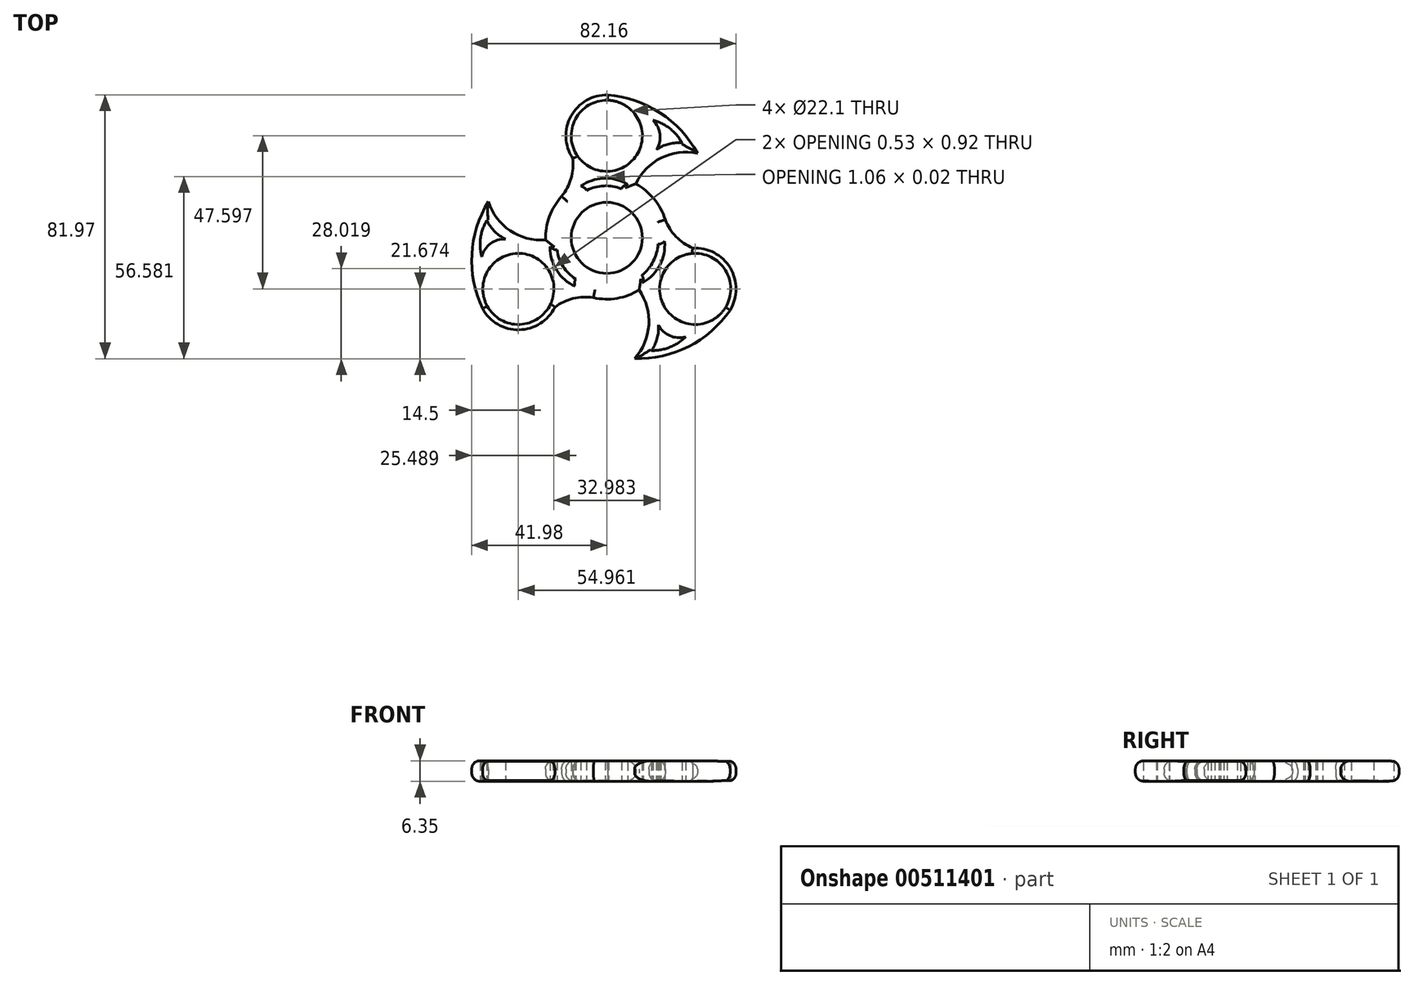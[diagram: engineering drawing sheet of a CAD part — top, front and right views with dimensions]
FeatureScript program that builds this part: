
annotation { "Feature Type Name" : "Feature", "Feature Type Description" : "" }
export const myFeature = defineFeature(function(context is Context, id is Id, definition is map)
    precondition{}
    {
        {
            var Q0;
            Q0=qCreatedBy(makeId("Top.planeOp"),FACE);
            var sketch = newSketch(context, id + "F0", { "sketchPlane" : qUnion([Q0])});
            skCircle(sketch, "E0", {"center": v(0, 0) * mm, "radius": 11.05 * mm});
            skCircle(sketch, "E1", {"center": v(0, 0) * mm, "radius": 44.45 * mm});
            skCircle(sketch, "E2", {"center": v(0, 31.73) * mm, "radius": 11.05 * mm});
            skArc(sketch, "E3", {"start": v(2.6, 44.16) * mm, "mid": v(-10.5, 38.87) * mm, "end": v(-10.6, 24.73) * mm});
            skCircle(sketch, "E4.1.0", {"center": v(-27.48, -15.87) * mm, "radius": 11.05 * mm});
            skArc(sketch, "E4.1.1", {"start": v(-39.55, -19.82) * mm, "mid": v(-28.41, -28.53) * mm, "end": v(-16.12, -21.54) * mm});
            skCircle(sketch, "E4.2.0", {"center": v(27.48, -15.87) * mm, "radius": 11.05 * mm});
            skArc(sketch, "E4.2.1", {"start": v(16.76, -9.06) * mm, "mid": v(16.48, -9.52) * mm, "end": v(16.23, -9.98) * mm});
            skArc(sketch, "E5", {"start": v(28.18, 26.24) * mm, "mid": v(16.42, 38.95) * mm, "end": v(0, 44.45) * mm});
            skArc(sketch, "E6", {"start": v(28.18, 26.24) * mm, "mid": v(16.94, 24.86) * mm, "end": v(9, 16.8) * mm});
            skArc(sketch, "E7.0", {"start": v(-14.02, 12.9) * mm, "mid": v(-17.86, 6.64) * mm, "end": v(-19.04, -0.61) * mm});
            skArc(sketch, "E8", {"start": v(-4.16, -18.6) * mm, "mid": v(-10.44, -18.85) * mm, "end": v(-16.12, -21.54) * mm});
            skArc(sketch, "E9.1.0", {"start": v(-36.82, 11.28) * mm, "mid": v(-41.94, -5.26) * mm, "end": v(-38.5, -22.22) * mm});
            skArc(sketch, "E9.1.1", {"start": v(-36.82, 11.28) * mm, "mid": v(-30, 2.24) * mm, "end": v(-19.04, -0.61) * mm});
            skArc(sketch, "E9.1.2", {"start": v(18.18, 5.7) * mm, "mid": v(21.54, 0.38) * mm, "end": v(26.72, -3.19) * mm});
            skArc(sketch, "E9.2.0", {"start": v(8.64, -37.52) * mm, "mid": v(25.52, -33.7) * mm, "end": v(38.5, -22.23) * mm});
            skArc(sketch, "E9.2.1", {"start": v(8.64, -37.52) * mm, "mid": v(13.06, -27.1) * mm, "end": v(10.05, -16.18) * mm});
            skArc(sketch, "E9.2.2", {"start": v(-14.02, 12.9) * mm, "mid": v(-11.1, 18.47) * mm, "end": v(-10.6, 24.73) * mm});
            skArc(sketch, "E10.trimOffspring", {"start": v(0.53, 19.04) * mm, "mid": v(0, 19.05) * mm, "end": v(-0.53, 19.04) * mm});
            skArc(sketch, "E11.trimOffspring", {"start": v(18.18, 5.7) * mm, "mid": v(14.68, 12.15) * mm, "end": v(9, 16.8) * mm});
            skArc(sketch, "E12.trimOffspring", {"start": v(16.23, -9.98) * mm, "mid": v(16.5, -9.53) * mm, "end": v(16.76, -9.06) * mm});
            skArc(sketch, "E13.trimOffspring", {"start": v(-4.16, -18.6) * mm, "mid": v(3.18, -18.78) * mm, "end": v(10.05, -16.18) * mm});
            skArc(sketch, "E14.trimOffspring", {"start": v(-16.76, -9.06) * mm, "mid": v(-16.5, -9.52) * mm, "end": v(-16.23, -9.98) * mm});
            skArc(sketch, "E15", {"start": v(6.5, 16.58) * mm, "mid": v(-0.86, 18.52) * mm, "end": v(-8.07, 16.08) * mm});
            skArc(sketch, "E16", {"start": v(-6.27, 14.78) * mm, "mid": v(-7.03, 15.62) * mm, "end": v(-8.07, 16.08) * mm});
            skArc(sketch, "E17", {"start": v(4.58, 15.27) * mm, "mid": v(-0.9, 16.16) * mm, "end": v(-6.27, 14.78) * mm});
            skArc(sketch, "E18", {"start": v(6.5, 16.58) * mm, "mid": v(5.35, 16.2) * mm, "end": v(4.58, 15.27) * mm});
            skArc(sketch, "E19.1.0", {"start": v(-17.6, -2.66) * mm, "mid": v(-15.6, -10) * mm, "end": v(-9.9, -15.03) * mm});
            skArc(sketch, "E19.1.1", {"start": v(-17.6, -2.66) * mm, "mid": v(-16.7, -3.46) * mm, "end": v(-15.51, -3.67) * mm});
            skArc(sketch, "E19.1.2", {"start": v(-15.51, -3.67) * mm, "mid": v(-13.55, -8.86) * mm, "end": v(-9.66, -12.82) * mm});
            skArc(sketch, "E19.1.3", {"start": v(-9.66, -12.82) * mm, "mid": v(-10.01, -13.9) * mm, "end": v(-9.9, -15.03) * mm});
            skArc(sketch, "E19.2.0", {"start": v(11.1, -13.92) * mm, "mid": v(16.47, -8.51) * mm, "end": v(17.96, -1.05) * mm});
            skArc(sketch, "E19.2.1", {"start": v(11.1, -13.92) * mm, "mid": v(11.35, -12.73) * mm, "end": v(10.94, -11.6) * mm});
            skArc(sketch, "E19.2.2", {"start": v(10.94, -11.6) * mm, "mid": v(14.45, -7.3) * mm, "end": v(15.93, -1.96) * mm});
            skArc(sketch, "E19.2.3", {"start": v(15.93, -1.96) * mm, "mid": v(17.04, -1.72) * mm, "end": v(17.96, -1.05) * mm});
            skArc(sketch, "E20", {"start": v(15.42, 27.42) * mm, "mid": v(16.54, 32.2) * mm, "end": v(14.36, 36.58) * mm});
            skArc(sketch, "E21", {"start": v(23.36, 29.54) * mm, "mid": v(19.6, 34) * mm, "end": v(14.36, 36.58) * mm});
            skArc(sketch, "E22", {"start": v(23.36, 29.54) * mm, "mid": v(19.2, 29.17) * mm, "end": v(15.42, 27.42) * mm});
            skArc(sketch, "E23.1.0", {"start": v(-37.27, 5.46) * mm, "mid": v(-34.87, 2.05) * mm, "end": v(-31.45, -0.35) * mm});
            skArc(sketch, "E23.1.1", {"start": v(-31.45, -0.35) * mm, "mid": v(-36.15, -1.77) * mm, "end": v(-38.86, -5.86) * mm});
            skArc(sketch, "E23.1.2", {"start": v(-37.27, 5.46) * mm, "mid": v(-39.24, -0.03) * mm, "end": v(-38.86, -5.86) * mm});
            skArc(sketch, "E23.2.0", {"start": v(13.9, -35) * mm, "mid": v(15.66, -31.22) * mm, "end": v(16.03, -27.06) * mm});
            skArc(sketch, "E23.2.1", {"start": v(16.03, -27.06) * mm, "mid": v(19.6, -30.42) * mm, "end": v(24.5, -30.73) * mm});
            skArc(sketch, "E23.2.2", {"start": v(13.9, -35) * mm, "mid": v(19.65, -33.97) * mm, "end": v(24.5, -30.73) * mm});
            skArc(sketch, "E24.trimOffspring", {"start": v(-0.53, 19.04) * mm, "mid": v(0, 19.03) * mm, "end": v(0.53, 19.04) * mm});
            skArc(sketch, "E25.trimOffspring", {"start": v(36.94, -24.34) * mm, "mid": v(38.91, -10.34) * mm, "end": v(26.72, -3.19) * mm});
            skArc(sketch, "E26.trimOffspring", {"start": v(-16.23, -9.98) * mm, "mid": v(-16.48, -9.52) * mm, "end": v(-16.76, -9.06) * mm});
            skSolve(sketch);
        }
        {
            var Q0;
            Q0=makeQuery(id+"F0.imprint","IMPRINT",FACE,{"disambiguationData":[TD([[makeQuery(id+"F0.imprint","IMPRINT",EDGE,{"derivedFrom":sQuery(id+"F0.wireOp",EDGE,"E0")}),-1.0]])]});
            extrude(context, id + "F1", {"entities" : qUnion([Q0]), "depth" : 6.35 * mm});
        }
        {
            var Q0;
            Q0=makeQuery(id+"F1.opExtrude","CAP_EDGE",EDGE,{"disambiguationData":[OSD([sQuery(id+"F0.wireOp",EDGE,"E9.2.0")])],"isStart":false});
            var Q1;
            Q1=makeQuery(id+"F1.opExtrude","CAP_EDGE",EDGE,{"disambiguationData":[OSD([sQuery(id+"F0.wireOp",EDGE,"E25.trimOffspring")])],"isStart":false});
            var Q2;
            Q2=makeQuery(id+"F1.opExtrude","CAP_EDGE",EDGE,{"disambiguationData":[OSD([sQuery(id+"F0.wireOp",EDGE,"E9.1.2")])],"isStart":false});
            var Q3;
            Q3=makeQuery(id+"F1.opExtrude","CAP_EDGE",EDGE,{"disambiguationData":[OSD([sQuery(id+"F0.wireOp",EDGE,"E11.trimOffspring")])],"isStart":false});
            var Q4;
            Q4=makeQuery(id+"F1.opExtrude","CAP_EDGE",EDGE,{"disambiguationData":[OSD([sQuery(id+"F0.wireOp",EDGE,"E6")])],"isStart":false});
            var Q5;
            Q5=makeQuery(id+"F1.opExtrude","CAP_EDGE",EDGE,{"disambiguationData":[OSD([sQuery(id+"F0.wireOp",EDGE,"E5")])],"isStart":false});
            var Q6;
            Q6=makeQuery(id+"F1.opExtrude","CAP_EDGE",EDGE,{"disambiguationData":[OSD([sQuery(id+"F0.wireOp",EDGE,"E9.2.1")])],"isStart":false});
            var Q7;
            Q7=makeQuery(id+"F1.opExtrude","CAP_EDGE",EDGE,{"disambiguationData":[OSD([sQuery(id+"F0.wireOp",EDGE,"E13.trimOffspring")])],"isStart":false});
            var Q8;
            Q8=makeQuery(id+"F1.opExtrude","CAP_EDGE",EDGE,{"disambiguationData":[OSD([sQuery(id+"F0.wireOp",EDGE,"E4.1.1")])],"isStart":false});
            var Q9;
            Q9=makeQuery(id+"F1.opExtrude","CAP_EDGE",EDGE,{"disambiguationData":[OSD([sQuery(id+"F0.wireOp",EDGE,"E9.1.0")])],"isStart":false});
            var Q10;
            Q10=makeQuery(id+"F1.opExtrude","CAP_EDGE",EDGE,{"disambiguationData":[OSD([sQuery(id+"F0.wireOp",EDGE,"E9.1.1")])],"isStart":false});
            var Q11;
            Q11=makeQuery(id+"F1.opExtrude","CAP_EDGE",EDGE,{"disambiguationData":[OSD([sQuery(id+"F0.wireOp",EDGE,"E7.0")])],"isStart":false});
            var Q12;
            Q12=makeQuery(id+"F1.opExtrude","CAP_EDGE",EDGE,{"disambiguationData":[OSD([sQuery(id+"F0.wireOp",EDGE,"E9.2.2")])],"isStart":false});
            var Q13;
            Q13=makeQuery(id+"F1.opExtrude","CAP_EDGE",EDGE,{"disambiguationData":[OSD([sQuery(id+"F0.wireOp",EDGE,"E3")])],"isStart":false});
            var Q14;
            Q14=makeQuery(id+"F1.opExtrude","CAP_EDGE",EDGE,{"disambiguationData":[OSD([sQuery(id+"F0.wireOp",EDGE,"E8")])],"isStart":false});
            var Q15;
            Q15=makeQuery(id+"F1.opExtrude","CAP_EDGE",EDGE,{"disambiguationData":[OSD([sQuery(id+"F0.wireOp",EDGE,"E9.2.0")])],"isStart":true});
            var Q16;
            Q16=makeQuery(id+"F1.opExtrude","CAP_EDGE",EDGE,{"disambiguationData":[OSD([sQuery(id+"F0.wireOp",EDGE,"E25.trimOffspring")])],"isStart":true});
            var Q17;
            Q17=makeQuery(id+"F1.opExtrude","CAP_EDGE",EDGE,{"disambiguationData":[OSD([sQuery(id+"F0.wireOp",EDGE,"E9.1.2")])],"isStart":true});
            var Q18;
            Q18=makeQuery(id+"F1.opExtrude","CAP_EDGE",EDGE,{"disambiguationData":[OSD([sQuery(id+"F0.wireOp",EDGE,"E11.trimOffspring")])],"isStart":true});
            var Q19;
            Q19=makeQuery(id+"F1.opExtrude","CAP_EDGE",EDGE,{"disambiguationData":[OSD([sQuery(id+"F0.wireOp",EDGE,"E6")])],"isStart":true});
            var Q20;
            Q20=makeQuery(id+"F1.opExtrude","CAP_EDGE",EDGE,{"disambiguationData":[OSD([sQuery(id+"F0.wireOp",EDGE,"E5")])],"isStart":true});
            var Q21;
            Q21=makeQuery(id+"F1.opExtrude","CAP_EDGE",EDGE,{"disambiguationData":[OSD([sQuery(id+"F0.wireOp",EDGE,"E3")])],"isStart":true});
            var Q22;
            Q22=makeQuery(id+"F1.opExtrude","CAP_EDGE",EDGE,{"disambiguationData":[OSD([sQuery(id+"F0.wireOp",EDGE,"E9.2.2")])],"isStart":true});
            var Q23;
            Q23=makeQuery(id+"F1.opExtrude","CAP_EDGE",EDGE,{"disambiguationData":[OSD([sQuery(id+"F0.wireOp",EDGE,"E7.0")])],"isStart":true});
            var Q24;
            Q24=makeQuery(id+"F1.opExtrude","CAP_EDGE",EDGE,{"disambiguationData":[OSD([sQuery(id+"F0.wireOp",EDGE,"E9.1.1")])],"isStart":true});
            var Q25;
            Q25=makeQuery(id+"F1.opExtrude","CAP_EDGE",EDGE,{"disambiguationData":[OSD([sQuery(id+"F0.wireOp",EDGE,"E9.1.0")])],"isStart":true});
            var Q26;
            Q26=makeQuery(id+"F1.opExtrude","CAP_EDGE",EDGE,{"disambiguationData":[OSD([sQuery(id+"F0.wireOp",EDGE,"E4.1.1")])],"isStart":true});
            var Q27;
            Q27=makeQuery(id+"F1.opExtrude","CAP_EDGE",EDGE,{"disambiguationData":[OSD([sQuery(id+"F0.wireOp",EDGE,"E8")])],"isStart":true});
            var Q28;
            Q28=makeQuery(id+"F1.opExtrude","CAP_EDGE",EDGE,{"disambiguationData":[OSD([sQuery(id+"F0.wireOp",EDGE,"E13.trimOffspring")])],"isStart":true});
            var Q29;
            Q29=makeQuery(id+"F1.opExtrude","CAP_EDGE",EDGE,{"disambiguationData":[OSD([sQuery(id+"F0.wireOp",EDGE,"E9.2.1")])],"isStart":true});
            fillet(context, id + "F2", {"entities" : qUnion([Q0, Q1, Q2, Q3, Q4, Q5, Q6, Q7, Q8, Q9, Q10, Q11, Q12, Q13, Q14, Q15, Q16, Q17, Q18, Q19, Q20, Q21, Q22, Q23, Q24, Q25, Q26, Q27, Q28, Q29]), "radius" : 2.54 * mm, "tangentPropagation" : true, "allowEdgeOverflow" : false});
        }
    });
